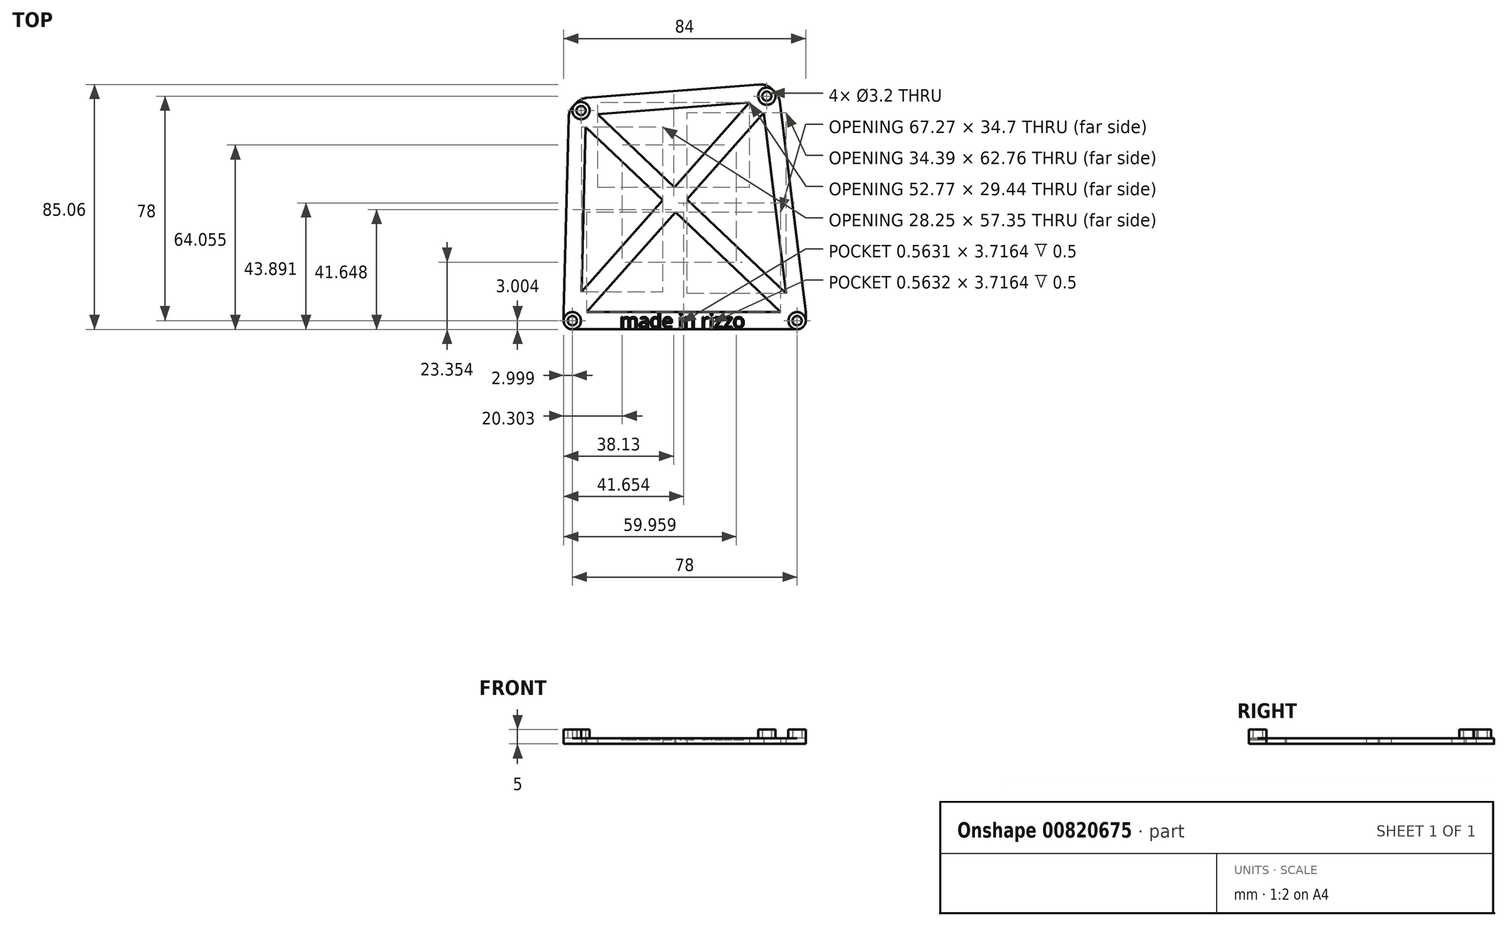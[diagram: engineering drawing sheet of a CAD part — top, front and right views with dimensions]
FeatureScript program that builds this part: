
annotation { "Feature Type Name" : "Feature", "Feature Type Description" : "" }
export const myFeature = defineFeature(function(context is Context, id is Id, definition is map)
    precondition{}
    {
        {
            var Q0;
            Q0=qCreatedBy(makeId("Top.planeOp"),FACE);
            var sketch = newSketch(context, id + "F0", { "sketchPlane" : qUnion([Q0])});
            skLineSegment(sketch, "E0", {"start": v(-34.24, -25.27) * mm, "end": v(49.76, -25.27) * mm});
            skLineSegment(sketch, "E1", {"start": v(-34.24, -25.27) * mm, "end": v(-34.24, -19.27) * mm});
            skLineSegment(sketch, "E2", {"start": v(-26.22, -19.27) * mm, "end": v(41.05, -19.27) * mm});
            skLineSegment(sketch, "E3", {"start": v(49.76, -19.27) * mm, "end": v(49.76, -25.27) * mm});
            skPoint(sketch, "E4", {"position": v(-31.24, -22.27) * mm});
            skPoint(sketch, "E5", {"position": v(46.76, -22.27) * mm});
            skPoint(sketch, "E6", {"position": v(-28.24, 50.73) * mm});
            skPoint(sketch, "E7", {"position": v(36.26, 55.73) * mm});
            skLineSegment(sketch, "E8", {"start": v(35.19, 50) * mm, "end": v(8.52, 19.93) * mm});
            skLineSegment(sketch, "E9", {"start": v(40.5, 55.99) * mm, "end": v(36, 59.97) * mm});
            skLineSegment(sketch, "E10", {"start": v(-28.06, -12.3) * mm, "end": v(0.2, 19.57) * mm});
            skLineSegment(sketch, "E11", {"start": v(42.91, -12.76) * mm, "end": v(8.52, 19.93) * mm});
            skLineSegment(sketch, "E12", {"start": v(-28.35, 54.98) * mm, "end": v(-32.48, 50.63) * mm});
            skLineSegment(sketch, "E13", {"start": v(-26.62, 45.05) * mm, "end": v(0.2, 19.57) * mm});
            skLineSegment(sketch, "E14.trimOffspring", {"start": v(4.54, 15.44) * mm, "end": v(-26.22, -19.27) * mm});
            skLineSegment(sketch, "E15.trimOffspring", {"start": v(4.54, 15.44) * mm, "end": v(41.05, -19.27) * mm});
            skLineSegment(sketch, "E16.trimOffspring", {"start": v(4.17, 24.06) * mm, "end": v(30.28, 53.5) * mm});
            skLineSegment(sketch, "E17.trimOffspring", {"start": v(4.17, 24.06) * mm, "end": v(-22.5, 49.41) * mm});
            skLineSegment(sketch, "E18", {"start": v(-32.48, 50.63) * mm, "end": v(-34.24, -19.27) * mm});
            skLineSegment(sketch, "E19", {"start": v(-28.35, 54.98) * mm, "end": v(36, 59.97) * mm});
            skLineSegment(sketch, "E20", {"start": v(40.5, 55.99) * mm, "end": v(49.76, -19.27) * mm});
            skLineSegment(sketch, "E21", {"start": v(-26.62, 45.05) * mm, "end": v(-28.01, -10.24) * mm});
            skLineSegment(sketch, "E22", {"start": v(-22.5, 49.41) * mm, "end": v(28.5, 53.37) * mm});
            skLineSegment(sketch, "E23", {"start": v(35.19, 50) * mm, "end": v(42.3, -7.8) * mm});
            skLineSegment(sketch, "E24", {"start": v(-27.95, -7.98) * mm, "end": v(-28.06, -12.3) * mm});
            skLineSegment(sketch, "E25", {"start": v(24.02, 53.02) * mm, "end": v(30.28, 53.5) * mm});
            skLineSegment(sketch, "E26", {"start": v(41.85, -4.1) * mm, "end": v(42.91, -12.76) * mm});
            skCircle(sketch, "E27", {"center": v(-28.24, 50.73) * mm, "radius": 3 * mm});
            skCircle(sketch, "E28", {"center": v(-28.24, 50.73) * mm, "radius": 1.6 * mm});
            skCircle(sketch, "E29", {"center": v(36.26, 55.73) * mm, "radius": 3 * mm});
            skCircle(sketch, "E30", {"center": v(36.26, 55.73) * mm, "radius": 1.6 * mm});
            skCircle(sketch, "E31", {"center": v(46.76, -22.27) * mm, "radius": 3 * mm});
            skCircle(sketch, "E32", {"center": v(46.76, -22.27) * mm, "radius": 1.6 * mm});
            skCircle(sketch, "E33", {"center": v(-31.24, -22.27) * mm, "radius": 3 * mm});
            skCircle(sketch, "E34", {"center": v(-31.24, -22.27) * mm, "radius": 1.6 * mm});
            skSolve(sketch);
        }
        {
            var Q0;
            Q0 = qSketchRegion(id + "F0", true);
            extrude(context, id + "F1", {"entities" : qUnion([Q0]), "depth" : 2 * mm, "offsetDistance" : 25 * mm});
        }
        {
            var Q0;
            Q0=makeQuery(id+"F0.imprint","IMPRINT",FACE,{"disambiguationData":[TD([[makeQuery(id+"F0.imprint","IMPRINT",EDGE,{"derivedFrom":sQuery(id+"F0.wireOp",EDGE,"E34")}),-1.0]])]});
            var Q1;
            Q1=makeQuery(id+"F0.imprint","IMPRINT",FACE,{"disambiguationData":[TD([[makeQuery(id+"F0.imprint","IMPRINT",EDGE,{"derivedFrom":sQuery(id+"F0.wireOp",EDGE,"E27")}),1.0]])]});
            var Q2;
            Q2=makeQuery(id+"F0.imprint","IMPRINT",FACE,{"disambiguationData":[TD([[makeQuery(id+"F0.imprint","IMPRINT",EDGE,{"derivedFrom":sQuery(id+"F0.wireOp",EDGE,"E29")}),1.0]])]});
            var Q3;
            Q3=makeQuery(id+"F0.imprint","IMPRINT",FACE,{"disambiguationData":[TD([[makeQuery(id+"F0.imprint","IMPRINT",EDGE,{"derivedFrom":sQuery(id+"F0.wireOp",EDGE,"E32")}),-1.0]])]});
            extrude(context, id + "F2", {"entities" : qUnion([Q0, Q1, Q2, Q3]), "operationType" : NewBodyOperationType.ADD, "depth" : 5 * mm, "offsetDistance" : 25 * mm});
        }
        {
            var Q0;
            {var subQ0=sQuery(id+"F0.wireOp",EDGE,"E26");var subQ1=sQuery(id+"F0.wireOp",EDGE,"E23");var subQ2=sQuery(id+"F0.wireOp",EDGE,"E25");var subQ3=sQuery(id+"F0.wireOp",EDGE,"E22");var subQ4=sQuery(id+"F0.wireOp",EDGE,"E24");var subQ5=sQuery(id+"F0.wireOp",EDGE,"E21");var subQ6=sQuery(id+"F0.wireOp",EDGE,"E20");var subQ7=sQuery(id+"F0.wireOp",EDGE,"E19");var subQ8=sQuery(id+"F0.wireOp",EDGE,"E18");var subQ9=sQuery(id+"F0.wireOp",EDGE,"E17.trimOffspring");var subQ10=sQuery(id+"F0.wireOp",EDGE,"E16.trimOffspring");var subQ11=sQuery(id+"F0.wireOp",EDGE,"E15.trimOffspring");var subQ12=sQuery(id+"F0.wireOp",EDGE,"E14.trimOffspring");var subQ13=sQuery(id+"F0.wireOp",EDGE,"E13");var subQ14=sQuery(id+"F0.wireOp",EDGE,"E2");var subQ15=sQuery(id+"F0.wireOp",EDGE,"E1");var subQ16=sQuery(id+"F0.wireOp",EDGE,"E12");var subQ17=sQuery(id+"F0.wireOp",EDGE,"E11");var subQ18=sQuery(id+"F0.wireOp",EDGE,"E10");var subQ19=sQuery(id+"F0.wireOp",EDGE,"E9");var subQ20=sQuery(id+"F0.wireOp",EDGE,"E8");var subQ21=sQuery(id+"F0.wireOp",EDGE,"E3");var subQ22=sQuery(id+"F0.wireOp",EDGE,"E0");var subQ23=makeQuery(id+"F1.opExtrude","CAP_FACE",FACE,{"disambiguationData":[OSD([subQ22,subQ15,subQ14,subQ21,subQ20,subQ19,subQ18,subQ17,subQ16,subQ13,subQ12,subQ11,subQ10,subQ9,subQ8,subQ7,subQ6,subQ5,subQ3,subQ1,subQ4,subQ2,subQ0,sQuery(id+"F0.wireOp",EDGE,"E28"),sQuery(id+"F0.wireOp",EDGE,"E30"),sQuery(id+"F0.wireOp",EDGE,"E32"),sQuery(id+"F0.wireOp",EDGE,"E34")])],"isStart":false});Q0=makeQuery(id+"F2.boolean.opBoolean","SPLIT",FACE,{"disambiguationData":[TD([makeQuery(id+"F1.opExtrude","SWEPT_FACE",FACE,{"disambiguationData":[OSD([subQ22])]}),subQ23,makeQuery(id+"F1.opExtrude","SWEPT_FACE",FACE,{"disambiguationData":[OSD([subQ15])]}),makeQuery(id+"F1.opExtrude","SWEPT_FACE",FACE,{"disambiguationData":[OSD([subQ14])]}),makeQuery(id+"F1.opExtrude","SWEPT_FACE",FACE,{"disambiguationData":[OSD([subQ21])]}),makeQuery(id+"F1.opExtrude","SWEPT_FACE",FACE,{"disambiguationData":[OSD([subQ20])]}),makeQuery(id+"F1.opExtrude","SWEPT_FACE",FACE,{"disambiguationData":[OSD([subQ19])]}),makeQuery(id+"F1.opExtrude","SWEPT_FACE",FACE,{"disambiguationData":[OSD([subQ18])]}),makeQuery(id+"F1.opExtrude","SWEPT_FACE",FACE,{"disambiguationData":[OSD([subQ17])]}),makeQuery(id+"F1.opExtrude","SWEPT_FACE",FACE,{"disambiguationData":[OSD([subQ16])]}),makeQuery(id+"F1.opExtrude","SWEPT_FACE",FACE,{"disambiguationData":[OSD([subQ13])]}),makeQuery(id+"F1.opExtrude","SWEPT_FACE",FACE,{"disambiguationData":[OSD([subQ12])]}),makeQuery(id+"F1.opExtrude","SWEPT_FACE",FACE,{"disambiguationData":[OSD([subQ11])]}),makeQuery(id+"F1.opExtrude","SWEPT_FACE",FACE,{"disambiguationData":[OSD([subQ10])]}),makeQuery(id+"F1.opExtrude","SWEPT_FACE",FACE,{"disambiguationData":[OSD([subQ9])]}),makeQuery(id+"F1.opExtrude","SWEPT_FACE",FACE,{"disambiguationData":[OSD([subQ8])]}),makeQuery(id+"F1.opExtrude","SWEPT_FACE",FACE,{"disambiguationData":[OSD([subQ7])]}),makeQuery(id+"F1.opExtrude","SWEPT_FACE",FACE,{"disambiguationData":[OSD([subQ6])]}),makeQuery(id+"F1.opExtrude","SWEPT_FACE",FACE,{"disambiguationData":[OSD([subQ5,subQ4])]}),makeQuery(id+"F1.opExtrude","SWEPT_FACE",FACE,{"disambiguationData":[OSD([subQ3,subQ2])]}),makeQuery(id+"F1.opExtrude","SWEPT_FACE",FACE,{"disambiguationData":[OSD([subQ1,subQ0])]}),makeQuery(id+"F2.opExtrude","SWEPT_FACE",FACE,{"disambiguationData":[OSD([sQuery(id+"F0.wireOp",EDGE,"E27")])]}),makeQuery(id+"F2.opExtrude","SWEPT_FACE",FACE,{"disambiguationData":[OSD([sQuery(id+"F0.wireOp",EDGE,"E29")])]}),makeQuery(id+"F2.opExtrude","SWEPT_FACE",FACE,{"disambiguationData":[OSD([sQuery(id+"F0.wireOp",EDGE,"E31")])]}),makeQuery(id+"F2.opExtrude","SWEPT_FACE",FACE,{"disambiguationData":[OSD([sQuery(id+"F0.wireOp",EDGE,"E33")])]})])],"derivedFrom":subQ23});}
            var sketch = newSketch(context, id + "F3", { "sketchPlane" : qUnion([Q0])});
            skText(sketch, "E35", { "text": "made in rizzo", "fontName": "OpenSans-Regular.ttf"});
            const initialGuessF3  = {"E35": [-0.01475, -0.02477, 1, 0, 0.005]};
            skSetInitialGuess(sketch, initialGuessF3);
            skSolve(sketch);
        }
        {
            var Q0;
            Q0 = qSketchRegion(id + "F3", true);
            extrude(context, id + "F4", {"entities" : qUnion([Q0]), "operationType" : NewBodyOperationType.REMOVE, "oppositeDirection" : true, "depth" : 0.5 * mm, "offsetDistance" : 25 * mm});
        }
        {
            var Q0;
            Q0=makeQuery(id+"F1.opExtrude","SWEPT_EDGE",EDGE,{"disambiguationData":[OSD([sQuery(id+"F0.wireOp",EDGE,"E0"),sQuery(id+"F0.wireOp",EDGE,"E1")])]});
            var Q1;
            Q1=makeQuery(id+"F1.opExtrude","SWEPT_EDGE",EDGE,{"disambiguationData":[OSD([sQuery(id+"F0.wireOp",EDGE,"E0"),sQuery(id+"F0.wireOp",EDGE,"E3")])]});
            fillet(context, id + "F5", {"entities" : qUnion([Q0, Q1]), "radius" : 3 * mm, "tangentPropagation" : true, "allowEdgeOverflow" : false});
        }
        {
            var Q0;
            Q0=makeQuery(id+"F1.opExtrude","SWEPT_EDGE",EDGE,{"disambiguationData":[OSD([sQuery(id+"F0.wireOp",EDGE,"E12"),sQuery(id+"F0.wireOp",EDGE,"E18")])]});
            var Q1;
            Q1=makeQuery(id+"F1.opExtrude","SWEPT_EDGE",EDGE,{"disambiguationData":[OSD([sQuery(id+"F0.wireOp",EDGE,"E12"),sQuery(id+"F0.wireOp",EDGE,"E19")])]});
            var Q2;
            Q2=makeQuery(id+"F1.opExtrude","SWEPT_EDGE",EDGE,{"disambiguationData":[OSD([sQuery(id+"F0.wireOp",EDGE,"E9"),sQuery(id+"F0.wireOp",EDGE,"E19")])]});
            var Q3;
            Q3=makeQuery(id+"F1.opExtrude","SWEPT_EDGE",EDGE,{"disambiguationData":[OSD([sQuery(id+"F0.wireOp",EDGE,"E9"),sQuery(id+"F0.wireOp",EDGE,"E20")])]});
            fillet(context, id + "F6", {"entities" : qUnion([Q0, Q1, Q2, Q3]), "radius" : 6 * mm, "tangentPropagation" : true, "allowEdgeOverflow" : false});
        }
    });
